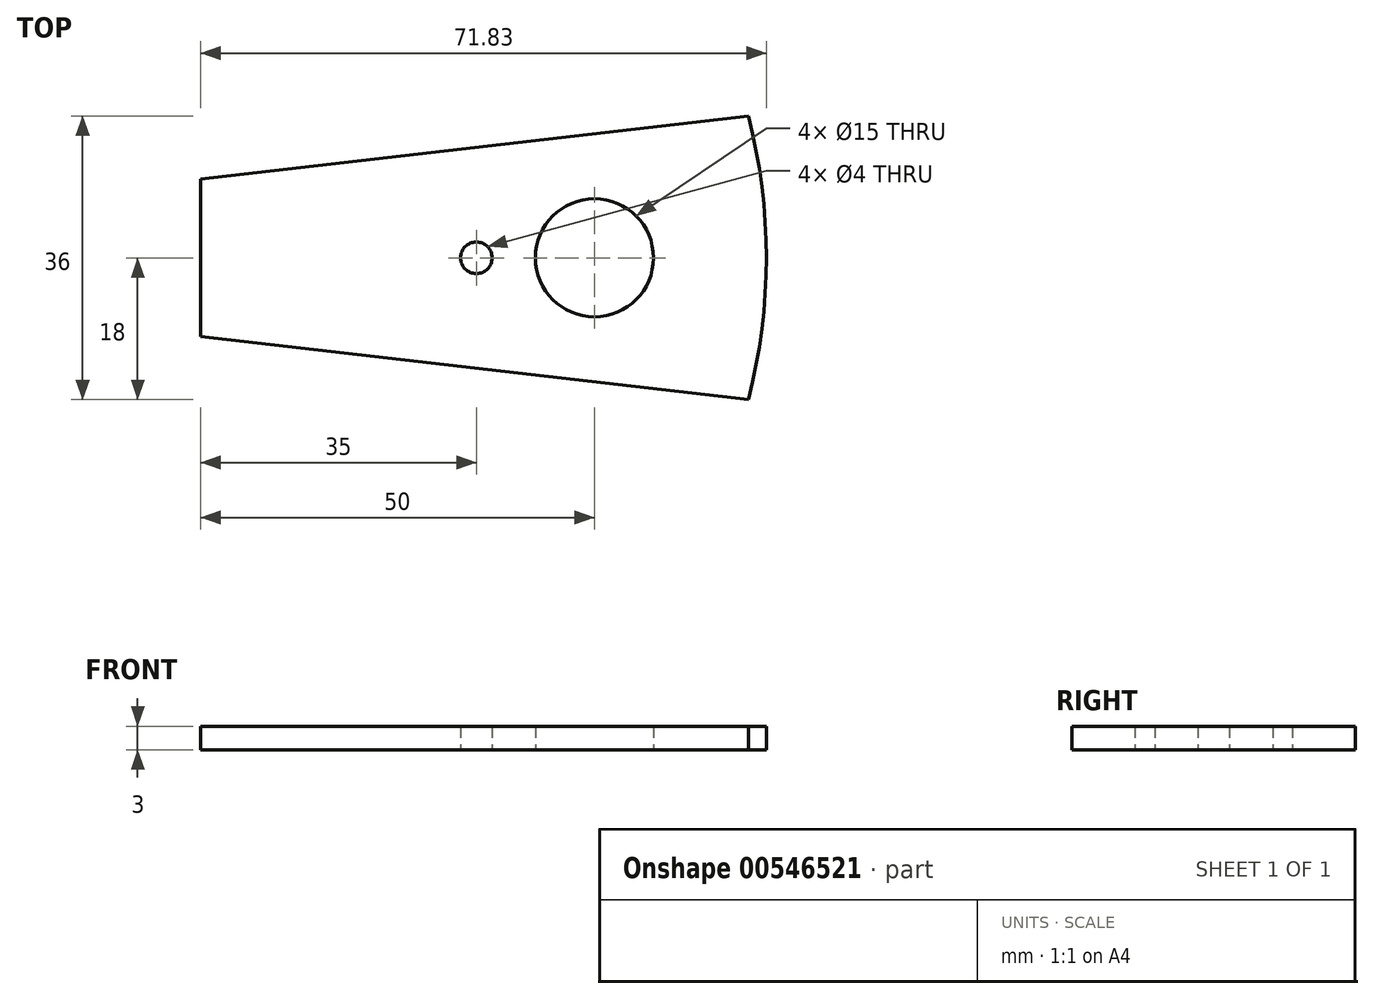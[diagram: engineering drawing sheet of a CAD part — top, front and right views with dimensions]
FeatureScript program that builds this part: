
annotation { "Feature Type Name" : "Feature", "Feature Type Description" : "" }
export const myFeature = defineFeature(function(context is Context, id is Id, definition is map)
    precondition{}
    {
        {
            var Q0;
            Q0=qCreatedBy(makeId("Top.planeOp"),FACE);
            var sketch = newSketch(context, id + "F0", { "sketchPlane" : qUnion([Q0])});
            skPoint(sketch, "E0", {"position": v(-35, 10) * mm});
            skPoint(sketch, "E1", {"position": v(-35, -10) * mm});
            skPoint(sketch, "E2", {"position": v(34.54, -18) * mm});
            skPoint(sketch, "E3", {"position": v(34.54, 18) * mm});
            skLineSegment(sketch, "E4", {"start": v(34.54, 18) * mm, "end": v(-35, 10) * mm});
            skLineSegment(sketch, "E5", {"start": v(-35, 10) * mm, "end": v(-35, -10) * mm});
            skLineSegment(sketch, "E6", {"start": v(-35, -10) * mm, "end": v(34.54, -18) * mm});
            skArc(sketch, "E7", {"start": v(34.54, -18) * mm, "mid": v(36.83, 0) * mm, "end": v(34.54, 18) * mm});
            skCircle(sketch, "E8", {"center": v(15, 0) * mm, "radius": 7.5 * mm});
            skCircle(sketch, "E9", {"center": v(0, 0) * mm, "radius": 2 * mm});
            skSolve(sketch);
        }
        {
            var Q0;
            Q0=makeQuery(id+"F0.imprint","IMPRINT",FACE,{"disambiguationData":[TD([[makeQuery(id+"F0.imprint","IMPRINT",EDGE,{"derivedFrom":sQuery(id+"F0.wireOp",EDGE,"E4")}),1.0]])]});
            extrude(context, id + "F1", {"entities" : qUnion([Q0]), "depth" : 3 * mm, "offsetDistance" : 25 * mm});
        }
    });
